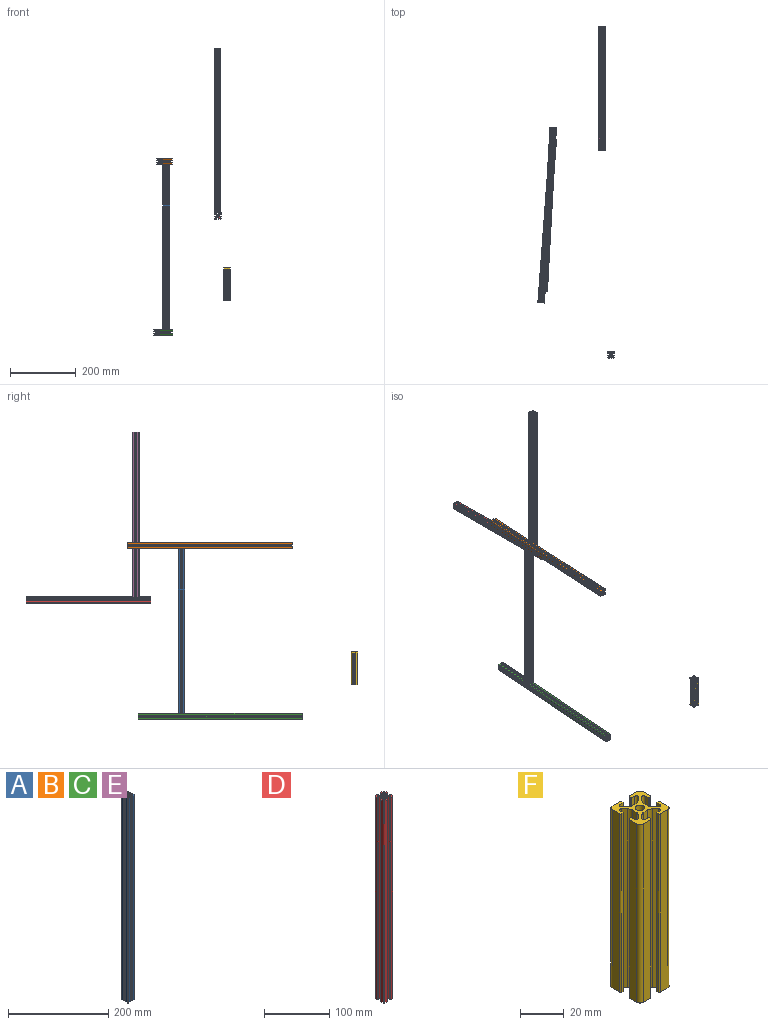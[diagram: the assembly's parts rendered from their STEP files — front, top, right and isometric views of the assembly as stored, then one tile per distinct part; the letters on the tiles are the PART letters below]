
ASSEMBLY  parts=6 mates=3
PART A: 75 faces, bbox 20x20x500 mm
  f0: plane 500x0.7mm, normal (0,1,0), area 350mm2, adj f1,f72,f73,f74
  f1: cylinder r=0.8mm len=500mm, axis (0,0,-1), area 628.3mm2, adj f0,f2,f73,f74
  f2: plane 500x4.7mm, normal (-1,0,0), area 2350mm2, adj f1,f3,f73,f74
  f3: cylinder r=2mm len=500mm, axis (0,0,-1), area 1570.8mm2, adj f2,f4,f73,f74
  f4: plane 500x4.7mm, normal (0,-1,0), area 2350mm2, adj f3,f5,f73,f74
  f5: cylinder r=0.8mm len=500mm, axis (0,0,-1), area 628.3mm2, adj f4,f6,f73,f74
  f6: plane 500x0.7mm, normal (1,0,0), area 350mm2, adj f5,f7,f73,f74
  f7: cylinder r=0.3mm len=500mm, axis (0,0,-1), area 235.6mm2, adj f6,f8,f73,f74
  f8: plane 500x2.12mm, normal (0,1,0), area 1058.8mm2, adj f7,f9,f73,f74
  f9: cylinder r=0.83mm len=500mm, axis (0,0,-1), area 980.7mm2, adj f8,f10,f73,f74
  f10: plane 500x2.25mm, normal (0.71,-0.71,0), area 1591.2mm2, adj f9,f11,f73,f74
  f11: cylinder r=3mm len=500mm, axis (0,0,-1), area 1178.1mm2, adj f10,f12,f73,f74
  f12: plane 500x2.27mm, normal (0,-1,0), area 1134.6mm2, adj f11,f13,f73,f74
  f13: cylinder r=3mm len=500mm, axis (0,0,-1), area 1178.1mm2, adj f12,f14,f73,f74
  f14: plane 500x2.25mm, normal (-0.71,-0.71,0), area 1591.2mm2, adj f13,f15,f73,f74
  f15: cylinder r=0.83mm len=500mm, axis (0,0,-1), area 980.7mm2, adj f14,f16,f73,f74
  f16: plane 500x2.12mm, normal (0,1,0), area 1058.8mm2, adj f15,f17,f73,f74
  f17: cylinder r=0.3mm len=500mm, axis (0,0,-1), area 235.6mm2, adj f16,f18,f73,f74
  f18: plane 500x0.7mm, normal (-1,0,0), area 350mm2, adj f17,f19,f73,f74
  f19: cylinder r=0.8mm len=500mm, axis (0,0,-1), area 628.3mm2, adj f18,f20,f73,f74
  f20: plane 500x4.7mm, normal (0,-1,0), area 2350mm2, adj f19,f21,f73,f74
  f21: cylinder r=2mm len=500mm, axis (0,0,-1), area 1570.8mm2, adj f20,f22,f73,f74
  f22: plane 500x4.7mm, normal (1,0,0), area 2350mm2, adj f21,f23,f73,f74
  f23: cylinder r=0.8mm len=500mm, axis (0,0,-1), area 628.3mm2, adj f22,f24,f73,f74
  f24: plane 500x0.7mm, normal (0,1,0), area 350mm2, adj f23,f25,f73,f74
  f25: cylinder r=0.3mm len=500mm, axis (0,0,-1), area 235.6mm2, adj f24,f26,f73,f74
  f26: plane 500x2.12mm, normal (-1,0,0), area 1058.8mm2, adj f25,f27,f73,f74
  f27: cylinder r=0.83mm len=500mm, axis (0,0,-1), area 980.7mm2, adj f26,f28,f73,f74
  f28: plane 500x2.25mm, normal (0.71,0.71,0), area 1591.2mm2, adj f27,f29,f73,f74
  f29: cylinder r=3mm len=500mm, axis (0,0,-1), area 1178.1mm2, adj f28,f30,f73,f74
  f30: plane 500x2.27mm, normal (1,0,0), area 1134.6mm2, adj f29,f31,f73,f74
  f31: cylinder r=3mm len=500mm, axis (0,0,-1), area 1178.1mm2, adj f30,f32,f73,f74
  f32: plane 500x2.25mm, normal (0.71,-0.71,0), area 1591.2mm2, adj f31,f33,f73,f74
  f33: cylinder r=0.83mm len=500mm, axis (0,0,-1), area 980.7mm2, adj f32,f34,f73,f74
  f34: plane 500x2.12mm, normal (-1,0,0), area 1058.8mm2, adj f33,f35,f73,f74
  f35: cylinder r=0.3mm len=500mm, axis (0,0,-1), area 235.6mm2, adj f34,f36,f73,f74
  f36: plane 500x0.7mm, normal (0,-1,0), area 350mm2, adj f35,f37,f73,f74
  f37: cylinder r=0.8mm len=500mm, axis (0,0,-1), area 628.3mm2, adj f36,f38,f73,f74
  f38: plane 500x4.7mm, normal (1,0,0), area 2350mm2, adj f37,f39,f73,f74
  f39: cylinder r=2mm len=500mm, axis (0,0,-1), area 1570.8mm2, adj f38,f40,f73,f74
  f40: plane 500x4.7mm, normal (0,1,0), area 2350mm2, adj f39,f41,f73,f74
  f41: cylinder r=0.8mm len=500mm, axis (0,0,-1), area 628.3mm2, adj f40,f42,f73,f74
  f42: plane 500x0.7mm, normal (-1,0,0), area 350mm2, adj f41,f43,f73,f74
  f43: cylinder r=0.3mm len=500mm, axis (0,0,-1), area 235.6mm2, adj f42,f44,f73,f74
  f44: plane 500x2.12mm, normal (0,-1,0), area 1058.8mm2, adj f43,f45,f73,f74
  f45: cylinder r=0.83mm len=500mm, axis (0,0,-1), area 980.7mm2, adj f44,f46,f73,f74
  f46: plane 500x2.25mm, normal (-0.71,0.71,0), area 1591.2mm2, adj f45,f47,f73,f74
  f47: cylinder r=3mm len=500mm, axis (0,0,-1), area 1178.1mm2, adj f46,f48,f73,f74
  f48: plane 500x2.27mm, normal (0,1,0), area 1134.6mm2, adj f47,f49,f73,f74
  f49: cylinder r=3mm len=500mm, axis (0,0,-1), area 1178.1mm2, adj f48,f50,f73,f74
  f50: plane 500x2.25mm, normal (0.71,0.71,0), area 1591.2mm2, adj f49,f51,f73,f74
  f51: cylinder r=0.83mm len=500mm, axis (0,0,-1), area 980.7mm2, adj f50,f52,f73,f74
  f52: plane 500x2.12mm, normal (0,-1,0), area 1058.8mm2, adj f51,f53,f73,f74
  f53: cylinder r=0.3mm len=500mm, axis (0,0,-1), area 235.6mm2, adj f52,f54,f73,f74
  f54: plane 500x0.7mm, normal (1,0,0), area 350mm2, adj f53,f55,f73,f74
  f55: cylinder r=0.8mm len=500mm, axis (0,0,-1), area 628.3mm2, adj f54,f56,f73,f74
  f56: plane 500x4.7mm, normal (0,1,0), area 2350mm2, adj f55,f57,f73,f74
  f57: cylinder r=2mm len=500mm, axis (0,0,-1), area 1570.8mm2, adj f56,f58,f73,f74
  f58: plane 500x4.7mm, normal (-1,0,0), area 2350mm2, adj f57,f59,f73,f74
  f59: cylinder r=0.8mm len=500mm, axis (0,0,-1), area 628.3mm2, adj f58,f60,f73,f74
  f60: plane 500x0.7mm, normal (0,-1,0), area 350mm2, adj f59,f61,f73,f74
  f61: cylinder r=0.3mm len=500mm, axis (0,0,-1), area 235.6mm2, adj f60,f62,f73,f74
  f62: plane 500x2.12mm, normal (1,0,0), area 1058.8mm2, adj f61,f63,f73,f74
  f63: cylinder r=0.83mm len=500mm, axis (0,0,-1), area 980.7mm2, adj f62,f64,f73,f74
  f64: plane 500x2.25mm, normal (-0.71,-0.71,0), area 1591.2mm2, adj f63,f65,f73,f74
  f65: cylinder r=3mm len=500mm, axis (0,0,-1), area 1178.1mm2, adj f64,f66,f73,f74
  f66: plane 500x2.27mm, normal (-1,0,0), area 1134.6mm2, adj f65,f67,f73,f74
  f67: cylinder r=3mm len=500mm, axis (0,0,-1), area 1178.1mm2, adj f66,f68,f73,f74
  f68: plane 500x2.25mm, normal (-0.71,0.71,0), area 1591.2mm2, adj f67,f69,f73,f74
  f69: cylinder r=0.83mm len=500mm, axis (0,0,-1), area 980.7mm2, adj f68,f70,f73,f74
  f70: plane 500x2.12mm, normal (1,0,0), area 1058.8mm2, adj f69,f72,f73,f74
  f71: cylinder r=2.15mm len=500mm, axis (0,0,-1), area 6754.4mm2, adj f73,f74
  f72: cylinder r=0.3mm len=500mm, axis (0,0,-1), area 235.6mm2, adj f0,f70,f73,f74
  f73: plane 20x20mm, normal (0,0,1), area 183.9mm2, adj f0,f1,f2,f3,f4,f5,f6,f7
  f74: plane 20x20mm, normal (0,0,-1), area 183.9mm2, adj f0,f1,f2,f3,f4,f5,f6,f7
PART B: same geometry as A
PART C: same geometry as A
PART D: 75 faces, bbox 20x20x380 mm
  f0: plane 380x0.7mm, normal (0,1,0), area 266mm2, adj f1,f72,f73,f74
  f1: cylinder r=0.8mm len=380mm, axis (0,0,-1), area 477.5mm2, adj f0,f2,f73,f74
  f2: plane 380x4.7mm, normal (-1,0,0), area 1786mm2, adj f1,f3,f73,f74
  f3: cylinder r=2mm len=380mm, axis (0,0,-1), area 1193.8mm2, adj f2,f4,f73,f74
  f4: plane 380x4.7mm, normal (0,-1,0), area 1786mm2, adj f3,f5,f73,f74
  f5: cylinder r=0.8mm len=380mm, axis (0,0,-1), area 477.5mm2, adj f4,f6,f73,f74
  f6: plane 380x0.7mm, normal (1,0,0), area 266mm2, adj f5,f7,f73,f74
  f7: cylinder r=0.3mm len=380mm, axis (0,0,-1), area 179.1mm2, adj f6,f8,f73,f74
  f8: plane 380x2.12mm, normal (0,1,0), area 804.7mm2, adj f7,f9,f73,f74
  f9: cylinder r=0.83mm len=380mm, axis (0,0,-1), area 745.3mm2, adj f8,f10,f73,f74
  f10: plane 380x2.25mm, normal (0.71,-0.71,0), area 1209.3mm2, adj f9,f11,f73,f74
  f11: cylinder r=3mm len=380mm, axis (0,0,-1), area 895.4mm2, adj f10,f12,f73,f74
  f12: plane 380x2.27mm, normal (0,-1,0), area 862.3mm2, adj f11,f13,f73,f74
  f13: cylinder r=3mm len=380mm, axis (0,0,-1), area 895.4mm2, adj f12,f14,f73,f74
  f14: plane 380x2.25mm, normal (-0.71,-0.71,0), area 1209.3mm2, adj f13,f15,f73,f74
  f15: cylinder r=0.83mm len=380mm, axis (0,0,-1), area 745.3mm2, adj f14,f16,f73,f74
  f16: plane 380x2.12mm, normal (0,1,0), area 804.7mm2, adj f15,f17,f73,f74
  f17: cylinder r=0.3mm len=380mm, axis (0,0,-1), area 179.1mm2, adj f16,f18,f73,f74
  f18: plane 380x0.7mm, normal (-1,0,0), area 266mm2, adj f17,f19,f73,f74
  f19: cylinder r=0.8mm len=380mm, axis (0,0,-1), area 477.5mm2, adj f18,f20,f73,f74
  f20: plane 380x4.7mm, normal (0,-1,0), area 1786mm2, adj f19,f21,f73,f74
  f21: cylinder r=2mm len=380mm, axis (0,0,-1), area 1193.8mm2, adj f20,f22,f73,f74
  f22: plane 380x4.7mm, normal (1,0,0), area 1786mm2, adj f21,f23,f73,f74
  f23: cylinder r=0.8mm len=380mm, axis (0,0,-1), area 477.5mm2, adj f22,f24,f73,f74
  f24: plane 380x0.7mm, normal (0,1,0), area 266mm2, adj f23,f25,f73,f74
  f25: cylinder r=0.3mm len=380mm, axis (0,0,-1), area 179.1mm2, adj f24,f26,f73,f74
  f26: plane 380x2.12mm, normal (-1,0,0), area 804.7mm2, adj f25,f27,f73,f74
  f27: cylinder r=0.83mm len=380mm, axis (0,0,-1), area 745.3mm2, adj f26,f28,f73,f74
  f28: plane 380x2.25mm, normal (0.71,0.71,0), area 1209.3mm2, adj f27,f29,f73,f74
  f29: cylinder r=3mm len=380mm, axis (0,0,-1), area 895.4mm2, adj f28,f30,f73,f74
  f30: plane 380x2.27mm, normal (1,0,0), area 862.3mm2, adj f29,f31,f73,f74
  f31: cylinder r=3mm len=380mm, axis (0,0,-1), area 895.4mm2, adj f30,f32,f73,f74
  f32: plane 380x2.25mm, normal (0.71,-0.71,0), area 1209.3mm2, adj f31,f33,f73,f74
  f33: cylinder r=0.83mm len=380mm, axis (0,0,-1), area 745.3mm2, adj f32,f34,f73,f74
  f34: plane 380x2.12mm, normal (-1,0,0), area 804.7mm2, adj f33,f35,f73,f74
  f35: cylinder r=0.3mm len=380mm, axis (0,0,-1), area 179.1mm2, adj f34,f36,f73,f74
  f36: plane 380x0.7mm, normal (0,-1,0), area 266mm2, adj f35,f37,f73,f74
  f37: cylinder r=0.8mm len=380mm, axis (0,0,-1), area 477.5mm2, adj f36,f38,f73,f74
  f38: plane 380x4.7mm, normal (1,0,0), area 1786mm2, adj f37,f39,f73,f74
  f39: cylinder r=2mm len=380mm, axis (0,0,-1), area 1193.8mm2, adj f38,f40,f73,f74
  f40: plane 380x4.7mm, normal (0,1,0), area 1786mm2, adj f39,f41,f73,f74
  f41: cylinder r=0.8mm len=380mm, axis (0,0,-1), area 477.5mm2, adj f40,f42,f73,f74
  f42: plane 380x0.7mm, normal (-1,0,0), area 266mm2, adj f41,f43,f73,f74
  f43: cylinder r=0.3mm len=380mm, axis (0,0,-1), area 179.1mm2, adj f42,f44,f73,f74
  f44: plane 380x2.12mm, normal (0,-1,0), area 804.7mm2, adj f43,f45,f73,f74
  f45: cylinder r=0.83mm len=380mm, axis (0,0,-1), area 745.3mm2, adj f44,f46,f73,f74
  f46: plane 380x2.25mm, normal (-0.71,0.71,0), area 1209.3mm2, adj f45,f47,f73,f74
  f47: cylinder r=3mm len=380mm, axis (0,0,-1), area 895.4mm2, adj f46,f48,f73,f74
  f48: plane 380x2.27mm, normal (0,1,0), area 862.3mm2, adj f47,f49,f73,f74
  f49: cylinder r=3mm len=380mm, axis (0,0,-1), area 895.4mm2, adj f48,f50,f73,f74
  f50: plane 380x2.25mm, normal (0.71,0.71,0), area 1209.3mm2, adj f49,f51,f73,f74
  f51: cylinder r=0.83mm len=380mm, axis (0,0,-1), area 745.3mm2, adj f50,f52,f73,f74
  f52: plane 380x2.12mm, normal (0,-1,0), area 804.7mm2, adj f51,f53,f73,f74
  f53: cylinder r=0.3mm len=380mm, axis (0,0,-1), area 179.1mm2, adj f52,f54,f73,f74
  f54: plane 380x0.7mm, normal (1,0,0), area 266mm2, adj f53,f55,f73,f74
  f55: cylinder r=0.8mm len=380mm, axis (0,0,-1), area 477.5mm2, adj f54,f56,f73,f74
  f56: plane 380x4.7mm, normal (0,1,0), area 1786mm2, adj f55,f57,f73,f74
  f57: cylinder r=2mm len=380mm, axis (0,0,-1), area 1193.8mm2, adj f56,f58,f73,f74
  f58: plane 380x4.7mm, normal (-1,0,0), area 1786mm2, adj f57,f59,f73,f74
  f59: cylinder r=0.8mm len=380mm, axis (0,0,-1), area 477.5mm2, adj f58,f60,f73,f74
  f60: plane 380x0.7mm, normal (0,-1,0), area 266mm2, adj f59,f61,f73,f74
  f61: cylinder r=0.3mm len=380mm, axis (0,0,-1), area 179.1mm2, adj f60,f62,f73,f74
  f62: plane 380x2.12mm, normal (1,0,0), area 804.7mm2, adj f61,f63,f73,f74
  f63: cylinder r=0.83mm len=380mm, axis (0,0,-1), area 745.3mm2, adj f62,f64,f73,f74
  f64: plane 380x2.25mm, normal (-0.71,-0.71,0), area 1209.3mm2, adj f63,f65,f73,f74
  f65: cylinder r=3mm len=380mm, axis (0,0,-1), area 895.4mm2, adj f64,f66,f73,f74
  f66: plane 380x2.27mm, normal (-1,0,0), area 862.3mm2, adj f65,f67,f73,f74
  f67: cylinder r=3mm len=380mm, axis (0,0,-1), area 895.4mm2, adj f66,f68,f73,f74
  f68: plane 380x2.25mm, normal (-0.71,0.71,0), area 1209.3mm2, adj f67,f69,f73,f74
  f69: cylinder r=0.83mm len=380mm, axis (0,0,-1), area 745.3mm2, adj f68,f70,f73,f74
  f70: plane 380x2.12mm, normal (1,0,0), area 804.7mm2, adj f69,f72,f73,f74
  f71: cylinder r=2.15mm len=380mm, axis (0,0,-1), area 5133.4mm2, adj f73,f74
  f72: cylinder r=0.3mm len=380mm, axis (0,0,-1), area 179.1mm2, adj f0,f70,f73,f74
  f73: plane 20x20mm, normal (0,0,1), area 183.9mm2, adj f0,f1,f2,f3,f4,f5,f6,f7
  f74: plane 20x20mm, normal (0,0,-1), area 183.9mm2, adj f0,f1,f2,f3,f4,f5,f6,f7
PART E: same geometry as A
PART F: 75 faces, bbox 20x20x100 mm
  f0: plane 100x0.7mm, normal (0,1,0), area 70mm2, adj f1,f72,f73,f74
  f1: cylinder r=0.8mm len=100mm, axis (0,0,-1), area 125.7mm2, adj f0,f2,f73,f74
  f2: plane 100x4.7mm, normal (-1,0,0), area 470mm2, adj f1,f3,f73,f74
  f3: cylinder r=2mm len=100mm, axis (0,0,-1), area 314.2mm2, adj f2,f4,f73,f74
  f4: plane 100x4.7mm, normal (0,-1,0), area 470mm2, adj f3,f5,f73,f74
  f5: cylinder r=0.8mm len=100mm, axis (0,0,-1), area 125.7mm2, adj f4,f6,f73,f74
  f6: plane 100x0.7mm, normal (1,0,0), area 70mm2, adj f5,f7,f73,f74
  f7: cylinder r=0.3mm len=100mm, axis (0,0,-1), area 47.1mm2, adj f6,f8,f73,f74
  f8: plane 100x2.12mm, normal (0,1,0), area 211.8mm2, adj f7,f9,f73,f74
  f9: cylinder r=0.83mm len=100mm, axis (0,0,-1), area 196.1mm2, adj f8,f10,f73,f74
  f10: plane 100x2.25mm, normal (0.71,-0.71,0), area 318.2mm2, adj f9,f11,f73,f74
  f11: cylinder r=3mm len=100mm, axis (0,0,-1), area 235.6mm2, adj f10,f12,f73,f74
  f12: plane 100x2.27mm, normal (0,-1,0), area 226.9mm2, adj f11,f13,f73,f74
  f13: cylinder r=3mm len=100mm, axis (0,0,-1), area 235.6mm2, adj f12,f14,f73,f74
  f14: plane 100x2.25mm, normal (-0.71,-0.71,0), area 318.2mm2, adj f13,f15,f73,f74
  f15: cylinder r=0.83mm len=100mm, axis (0,0,-1), area 196.1mm2, adj f14,f16,f73,f74
  f16: plane 100x2.12mm, normal (0,1,0), area 211.8mm2, adj f15,f17,f73,f74
  f17: cylinder r=0.3mm len=100mm, axis (0,0,-1), area 47.1mm2, adj f16,f18,f73,f74
  f18: plane 100x0.7mm, normal (-1,0,0), area 70mm2, adj f17,f19,f73,f74
  f19: cylinder r=0.8mm len=100mm, axis (0,0,-1), area 125.7mm2, adj f18,f20,f73,f74
  f20: plane 100x4.7mm, normal (0,-1,0), area 470mm2, adj f19,f21,f73,f74
  f21: cylinder r=2mm len=100mm, axis (0,0,-1), area 314.2mm2, adj f20,f22,f73,f74
  f22: plane 100x4.7mm, normal (1,0,0), area 470mm2, adj f21,f23,f73,f74
  f23: cylinder r=0.8mm len=100mm, axis (0,0,-1), area 125.7mm2, adj f22,f24,f73,f74
  f24: plane 100x0.7mm, normal (0,1,0), area 70mm2, adj f23,f25,f73,f74
  f25: cylinder r=0.3mm len=100mm, axis (0,0,-1), area 47.1mm2, adj f24,f26,f73,f74
  f26: plane 100x2.12mm, normal (-1,0,0), area 211.8mm2, adj f25,f27,f73,f74
  f27: cylinder r=0.83mm len=100mm, axis (0,0,-1), area 196.1mm2, adj f26,f28,f73,f74
  f28: plane 100x2.25mm, normal (0.71,0.71,0), area 318.2mm2, adj f27,f29,f73,f74
  f29: cylinder r=3mm len=100mm, axis (0,0,-1), area 235.6mm2, adj f28,f30,f73,f74
  f30: plane 100x2.27mm, normal (1,0,0), area 226.9mm2, adj f29,f31,f73,f74
  f31: cylinder r=3mm len=100mm, axis (0,0,-1), area 235.6mm2, adj f30,f32,f73,f74
  f32: plane 100x2.25mm, normal (0.71,-0.71,0), area 318.2mm2, adj f31,f33,f73,f74
  f33: cylinder r=0.83mm len=100mm, axis (0,0,-1), area 196.1mm2, adj f32,f34,f73,f74
  f34: plane 100x2.12mm, normal (-1,0,0), area 211.8mm2, adj f33,f35,f73,f74
  f35: cylinder r=0.3mm len=100mm, axis (0,0,-1), area 47.1mm2, adj f34,f36,f73,f74
  f36: plane 100x0.7mm, normal (0,-1,0), area 70mm2, adj f35,f37,f73,f74
  f37: cylinder r=0.8mm len=100mm, axis (0,0,-1), area 125.7mm2, adj f36,f38,f73,f74
  f38: plane 100x4.7mm, normal (1,0,0), area 470mm2, adj f37,f39,f73,f74
  f39: cylinder r=2mm len=100mm, axis (0,0,-1), area 314.2mm2, adj f38,f40,f73,f74
  f40: plane 100x4.7mm, normal (0,1,0), area 470mm2, adj f39,f41,f73,f74
  f41: cylinder r=0.8mm len=100mm, axis (0,0,-1), area 125.7mm2, adj f40,f42,f73,f74
  f42: plane 100x0.7mm, normal (-1,0,0), area 70mm2, adj f41,f43,f73,f74
  f43: cylinder r=0.3mm len=100mm, axis (0,0,-1), area 47.1mm2, adj f42,f44,f73,f74
  f44: plane 100x2.12mm, normal (0,-1,0), area 211.8mm2, adj f43,f45,f73,f74
  f45: cylinder r=0.83mm len=100mm, axis (0,0,-1), area 196.1mm2, adj f44,f46,f73,f74
  f46: plane 100x2.25mm, normal (-0.71,0.71,0), area 318.2mm2, adj f45,f47,f73,f74
  f47: cylinder r=3mm len=100mm, axis (0,0,-1), area 235.6mm2, adj f46,f48,f73,f74
  f48: plane 100x2.27mm, normal (0,1,0), area 226.9mm2, adj f47,f49,f73,f74
  f49: cylinder r=3mm len=100mm, axis (0,0,-1), area 235.6mm2, adj f48,f50,f73,f74
  f50: plane 100x2.25mm, normal (0.71,0.71,0), area 318.2mm2, adj f49,f51,f73,f74
  f51: cylinder r=0.83mm len=100mm, axis (0,0,-1), area 196.1mm2, adj f50,f52,f73,f74
  f52: plane 100x2.12mm, normal (0,-1,0), area 211.8mm2, adj f51,f53,f73,f74
  f53: cylinder r=0.3mm len=100mm, axis (0,0,-1), area 47.1mm2, adj f52,f54,f73,f74
  f54: plane 100x0.7mm, normal (1,0,0), area 70mm2, adj f53,f55,f73,f74
  f55: cylinder r=0.8mm len=100mm, axis (0,0,-1), area 125.7mm2, adj f54,f56,f73,f74
  f56: plane 100x4.7mm, normal (0,1,0), area 470mm2, adj f55,f57,f73,f74
  f57: cylinder r=2mm len=100mm, axis (0,0,-1), area 314.2mm2, adj f56,f58,f73,f74
  f58: plane 100x4.7mm, normal (-1,0,0), area 470mm2, adj f57,f59,f73,f74
  f59: cylinder r=0.8mm len=100mm, axis (0,0,-1), area 125.7mm2, adj f58,f60,f73,f74
  f60: plane 100x0.7mm, normal (0,-1,0), area 70mm2, adj f59,f61,f73,f74
  f61: cylinder r=0.3mm len=100mm, axis (0,0,-1), area 47.1mm2, adj f60,f62,f73,f74
  f62: plane 100x2.12mm, normal (1,0,0), area 211.8mm2, adj f61,f63,f73,f74
  f63: cylinder r=0.83mm len=100mm, axis (0,0,-1), area 196.1mm2, adj f62,f64,f73,f74
  f64: plane 100x2.25mm, normal (-0.71,-0.71,0), area 318.2mm2, adj f63,f65,f73,f74
  f65: cylinder r=3mm len=100mm, axis (0,0,-1), area 235.6mm2, adj f64,f66,f73,f74
  f66: plane 100x2.27mm, normal (-1,0,0), area 226.9mm2, adj f65,f67,f73,f74
  f67: cylinder r=3mm len=100mm, axis (0,0,-1), area 235.6mm2, adj f66,f68,f73,f74
  f68: plane 100x2.25mm, normal (-0.71,0.71,0), area 318.2mm2, adj f67,f69,f73,f74
  f69: cylinder r=0.83mm len=100mm, axis (0,0,-1), area 196.1mm2, adj f68,f70,f73,f74
  f70: plane 100x2.12mm, normal (1,0,0), area 211.8mm2, adj f69,f72,f73,f74
  f71: cylinder r=2.15mm len=100mm, axis (0,0,-1), area 1350.9mm2, adj f73,f74
  f72: cylinder r=0.3mm len=100mm, axis (0,0,-1), area 47.1mm2, adj f0,f70,f73,f74
  f73: plane 20x20mm, normal (0,0,1), area 183.9mm2, adj f0,f1,f2,f3,f4,f5,f6,f7
  f74: plane 20x20mm, normal (0,0,-1), area 183.9mm2, adj f0,f1,f2,f3,f4,f5,f6,f7
PLACE A rot(axis=(-0.73,-0.69,0),180deg) t=(-216.94,-138.87,1000.92)mm
PLACE B rot(axis=(-0.02,-0.71,0.71),177.8deg) t=(-208.09,24.73,1010.92)mm
PLACE C rot(axis=(-0.03,-0.71,0.71),177deg) t=(-207.77,-8.5,490.92)mm
PLACE D rot(axis=(0.58,0.58,-0.58),120deg) t=(-60.19,334.12,846.11)mm fixed
PLACE E rot(axis=(-0.72,-0.69,0),180deg) t=(-60.93,0.79,1356.11)mm
PLACE F t=(-32.56,-665.33,587.35)mm
MATE planar B.f40 <-> A.f3  axis (0,0,-1) through (-227.44,-224.58,1000.92)mm
MATE planar C.f20 <-> A.f39  axis (0,0,1) through (-231.94,-257.39,500.92)mm
MATE planar E.f73 <-> D.f2  axis (0,0,-1) through (-66.14,7.8,856.11)mm
